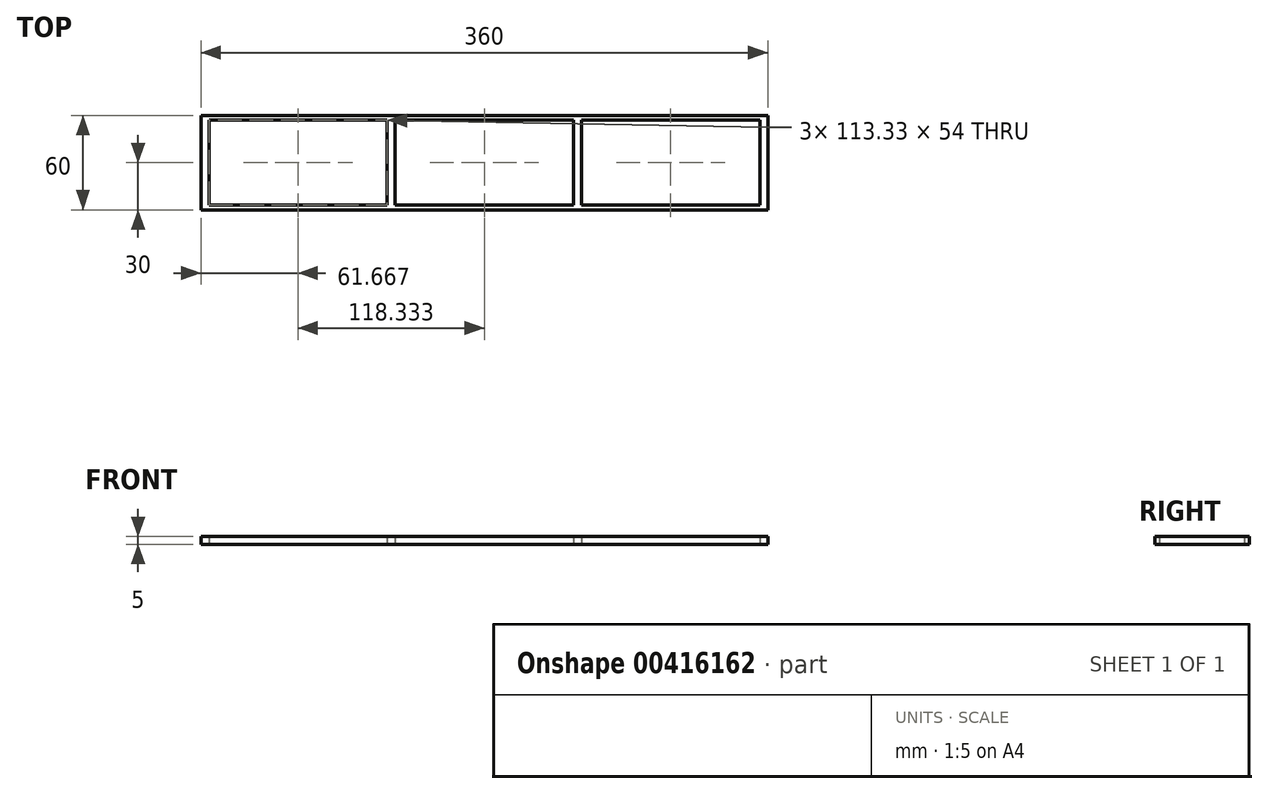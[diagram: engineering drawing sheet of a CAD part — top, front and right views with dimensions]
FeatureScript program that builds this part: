
annotation { "Feature Type Name" : "Feature", "Feature Type Description" : "" }
export const myFeature = defineFeature(function(context is Context, id is Id, definition is map)
    precondition{}
    {
        {
            var Q0;
            Q0=qCreatedBy(makeId("Top.planeOp"),FACE);
            var sketch = newSketch(context, id + "F0", { "sketchPlane" : qUnion([Q0])});
            skLineSegment(sketch, "E0.bottom", {"start": v(0, 0) * mm, "end": v(5, 0) * mm});
            skLineSegment(sketch, "E0.top", {"start": v(0, -30) * mm, "end": v(360, -30) * mm});
            skLineSegment(sketch, "E0.left", {"start": v(0, 0) * mm, "end": v(0, -30) * mm});
            skLineSegment(sketch, "E0.right", {"start": v(360, 0) * mm, "end": v(360, -30) * mm});
            skLineSegment(sketch, "E1.top", {"start": v(5, -27) * mm, "end": v(118.33, -27) * mm});
            skLineSegment(sketch, "E1.left", {"start": v(5, 0) * mm, "end": v(5, -27) * mm});
            skLineSegment(sketch, "E1.right", {"start": v(118.33, 0) * mm, "end": v(118.33, -27) * mm});
            skLineSegment(sketch, "E2.top", {"start": v(123.33, -27) * mm, "end": v(236.67, -27) * mm});
            skLineSegment(sketch, "E2.left", {"start": v(123.33, 0) * mm, "end": v(123.33, -27) * mm});
            skLineSegment(sketch, "E2.right", {"start": v(236.67, 0) * mm, "end": v(236.67, -27) * mm});
            skLineSegment(sketch, "E3.top", {"start": v(241.67, -27) * mm, "end": v(355, -27) * mm});
            skLineSegment(sketch, "E3.left", {"start": v(241.67, 0) * mm, "end": v(241.67, -27) * mm});
            skLineSegment(sketch, "E3.right", {"start": v(355, 0) * mm, "end": v(355, -27) * mm});
            skLineSegment(sketch, "E4.trimOffspring", {"start": v(118.33, 0) * mm, "end": v(123.33, 0) * mm});
            skLineSegment(sketch, "E5.trimOffspring", {"start": v(236.67, 0) * mm, "end": v(241.67, 0) * mm});
            skLineSegment(sketch, "E6.trimOffspring", {"start": v(355, 0) * mm, "end": v(360, 0) * mm});
            skSolve(sketch);
        }
        {
            var Q0;
            Q0 = qSketchRegion(id + "F0", true);
            extrude(context, id + "F1", {"entities" : qUnion([Q0]), "depth" : 5 * mm, "offsetDistance" : 25 * mm});
        }
        {
            var Q0;
            Q0=makeQuery(id+"F1.opExtrude","SWEPT_BODY",BODY,{"disambiguationData":[OSD([sQuery(id+"F0.wireOp",EDGE,"E0.bottom"),sQuery(id+"F0.wireOp",EDGE,"E0.top"),sQuery(id+"F0.wireOp",EDGE,"E0.left"),sQuery(id+"F0.wireOp",EDGE,"E0.right"),sQuery(id+"F0.wireOp",EDGE,"E1.top"),sQuery(id+"F0.wireOp",EDGE,"E1.left"),sQuery(id+"F0.wireOp",EDGE,"E1.right"),sQuery(id+"F0.wireOp",EDGE,"E2.top"),sQuery(id+"F0.wireOp",EDGE,"E2.left"),sQuery(id+"F0.wireOp",EDGE,"E2.right"),sQuery(id+"F0.wireOp",EDGE,"E3.top"),sQuery(id+"F0.wireOp",EDGE,"E3.left"),sQuery(id+"F0.wireOp",EDGE,"E3.right"),sQuery(id+"F0.wireOp",EDGE,"E4.trimOffspring"),sQuery(id+"F0.wireOp",EDGE,"E5.trimOffspring"),sQuery(id+"F0.wireOp",EDGE,"E6.trimOffspring")])]});
            var Q1;
            Q1=makeQuery(id+"F1.opExtrude","SWEPT_FACE",FACE,{"disambiguationData":[OSD([sQuery(id+"F0.wireOp",EDGE,"E0.bottom")])]});
            mirror(context, id + "F2", {"operationType" : NewBodyOperationType.ADD, "entities" : qUnion([Q0]), "mirrorPlane" : qUnion([Q1])});
        }
    });
